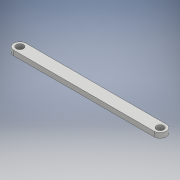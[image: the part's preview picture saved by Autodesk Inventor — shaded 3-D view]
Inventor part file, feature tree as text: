
AUTODESK INVENTOR PART (.ipt)
format: ipt  version: 2018 (Build 220112000, 112)  size: 101,376 bytes
history: native  units: mm
features: extrude x1, sketch x1
ambient origin geometry x8: Origin, YZ Plane, XZ Plane, XY Plane, X Axis, Y Axis, Z Axis, Center Point
bodies: Solid1 (feature_tree)
feature tree (2):
  extrude  "Extrusion1"  Depth=5.0mm
  sketch  "Sketch1"  dims[d0=57.756mm d1=5.0mm d2=3.0mm d3=0.5mm d4=2.0mm d5=0.0mm]
